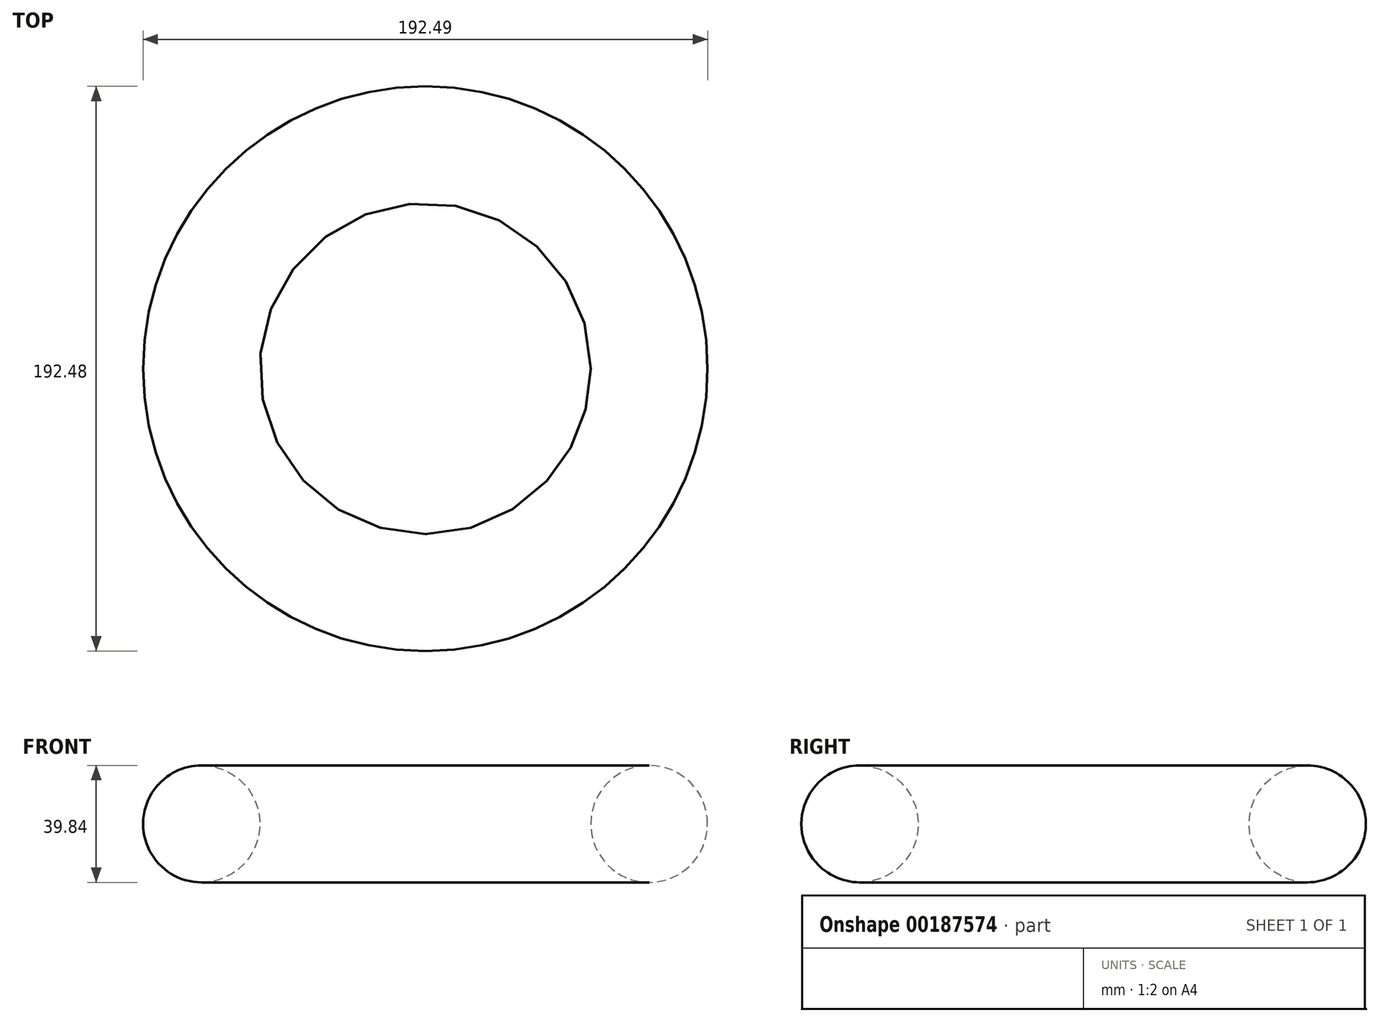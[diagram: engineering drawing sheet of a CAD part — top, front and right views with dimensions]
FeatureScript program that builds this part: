
annotation { "Feature Type Name" : "Feature", "Feature Type Description" : "" }
export const myFeature = defineFeature(function(context is Context, id is Id, definition is map)
    precondition{}
    {
        {
            var Q0;
            Q0=qCreatedBy(makeId("Front.planeOp"),FACE);
            var sketch = newSketch(context, id + "F0", { "sketchPlane" : qUnion([Q0])});
            skCircle(sketch, "E0", {"center": v(0, 0) * mm, "radius": 19.92 * mm});
            skPoint(sketch, "E1", {"position": v(-76.33, 0) * mm});
            skLineSegment(sketch, "E2", {"start": v(-76.33, 0) * mm, "end": v(-76.33, 44.18) * mm});
            skLineSegment(sketch, "E3", {"start": v(-76.33, 44.18) * mm, "end": v(-76.33, -42.29) * mm});
            skSolve(sketch);
        }
        {
            var Q0;
            Q0=makeQuery(id+"F0.imprint","IMPRINT",FACE,{"disambiguationData":[TD([[makeQuery(id+"F0.imprint","IMPRINT",EDGE,{"derivedFrom":sQuery(id+"F0.wireOp",EDGE,"E0")}),1.0]])]});
            var Q1;
            Q1=sQuery(id+"F0.wireOp",EDGE,"E3");
            revolve(context, id + "F1", {"entities" : qUnion([Q0]), "axis" : qUnion([Q1]), "revolveType" : RevolveType.FULL});
        }
    });
